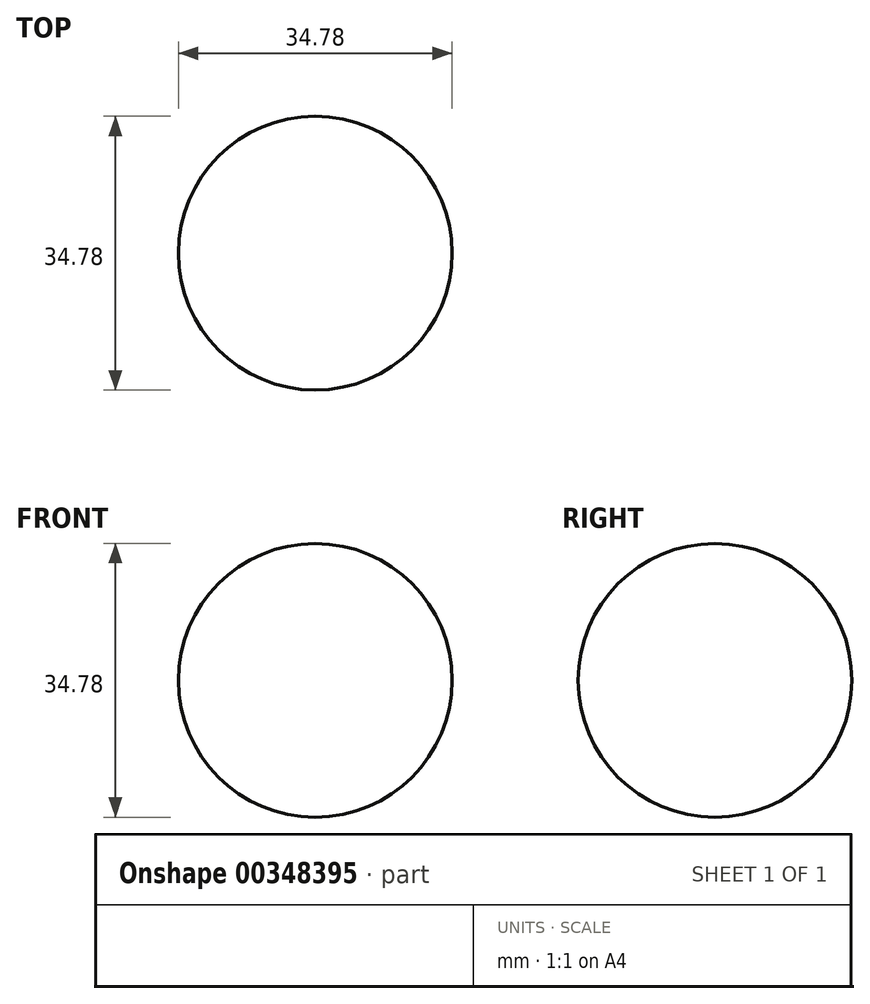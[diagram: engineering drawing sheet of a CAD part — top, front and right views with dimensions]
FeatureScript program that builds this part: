
annotation { "Feature Type Name" : "Feature", "Feature Type Description" : "" }
export const myFeature = defineFeature(function(context is Context, id is Id, definition is map)
    precondition{}
    {
        {
            var Q0;
            Q0=qCreatedBy(makeId("Right.planeOp"),FACE);
            var sketch = newSketch(context, id + "F0", { "sketchPlane" : qUnion([Q0])});
            skArc(sketch, "E0", {"start": v(0, -17.39) * mm, "mid": v(17.39, 0) * mm, "end": v(0, 17.39) * mm});
            skLineSegment(sketch, "E1", {"start": v(0, -25.4) * mm, "end": v(0, 23.5) * mm, "construction": true});
            skSolve(sketch);
        }
        {
            var Q0;
            Q0=sQuery(id+"F0.wireOp",EDGE,"E0");
            var Q1;
            Q1=sQuery(id+"F0.wireOp",EDGE,"E1");
            revolve(context, id + "F1", {"bodyType" : ToolBodyType.SURFACE, "surfaceEntities" : qUnion([Q0]), "axis" : qUnion([Q1]), "revolveType" : RevolveType.ONE_DIRECTION, "angle" : 360 * degree});
        }
    });
